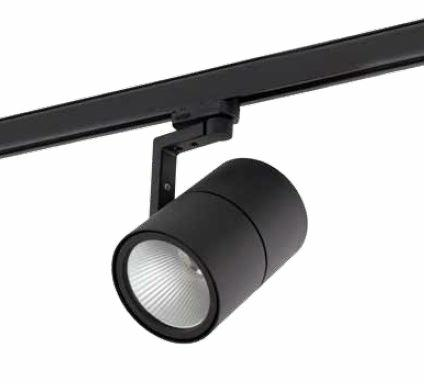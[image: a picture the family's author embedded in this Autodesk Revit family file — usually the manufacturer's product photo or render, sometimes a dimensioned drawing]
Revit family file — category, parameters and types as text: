
# Revit family: DS 1011 PLN (Ra90)
name_source: partatom
category: Lighting Fixtures
revit_build: Autodesk Revit 2017 (Build: 20160225_1515(x64)
units: mm (PartAtom-declared; Revit-internal decimal feet)

## family parameters
Cut with Voids When Loaded = No
Host = Face
Light Source = Yes
Part Type = Normal
Room Calculation Point = No
Round Connector Dimension = Use Diameter
Shared = No

## types (18) — shared parameters
Color Filter = 16777215
Default Elevation = 1219 mm
Dimming Lamp Color Temperature Shift = <None>
Emit Shape Visible in Rendering = Yes
Emit from Circle Diameter = 100 mm  [stored 0.328084 ft]
Light Source Symbol Length = 3048 mm  [stored 10 ft]
Manufacturer = ARLIGHT
Spot Field Angle = 90.00°
Tilt Angle = 90.00°
Type Image = DS 1011 PLN.JPG

## per-type parameters (varying)
| type | Spot Beam Angle | Wattage Comments |
| DSPLN.11.19.30.15.90 | 15.00° | 19 |
| DSPLN.11.19.40.15.90 | 15.00° | 19 |
| DSPLN.11.19.30.24.90 | 24.00° | 19 |
| DSPLN.11.19.40.24.90 | 24.00° | 19 |
| DSPLN.11.19.30.42.90 | 42.00° | 19 |
| DSPLN.11.19.40.42.90 | 42.00° | 19 |
| DSPLN.11.27.30.15.90 | 15.00° | 27 |
| DSPLN.11.27.40.15.90 | 15.00° | 27 |
| DSPLN.11.27.30.24.90 | 24.00° | 27 |
| DSPLN.11.27.30.42.90 | 42.00° | 27 |
| DSPLN.11.27.40.42.90 | 42.00° | 27 |
| DSPLN.11.35.30.15.90 | 15.00° | 35 |
| DSPLN.11.35.40.15.90 | 15.00° | 35 |
| DSPLN.11.35.30.24.90 | 24.00° | 35 |
| DSPLN.11.35.40.24.90 | 24.00° | 35 |
| DSPLN.11.35.30.42.90 | 42.00° | 35 |
| DSPLN.11.35.40.42.90 | 42.00° | 35 |
| DSPLN.11.27.40.24.90 | 24.00° | 27 |

note: [stored X ft] marks values corroborated as IEEE doubles in the binary element streams (Revit-internal decimal feet)

## geometry (parser evidence)
native form markers: Sweep x3
no freeform markers — native parametric forms only
